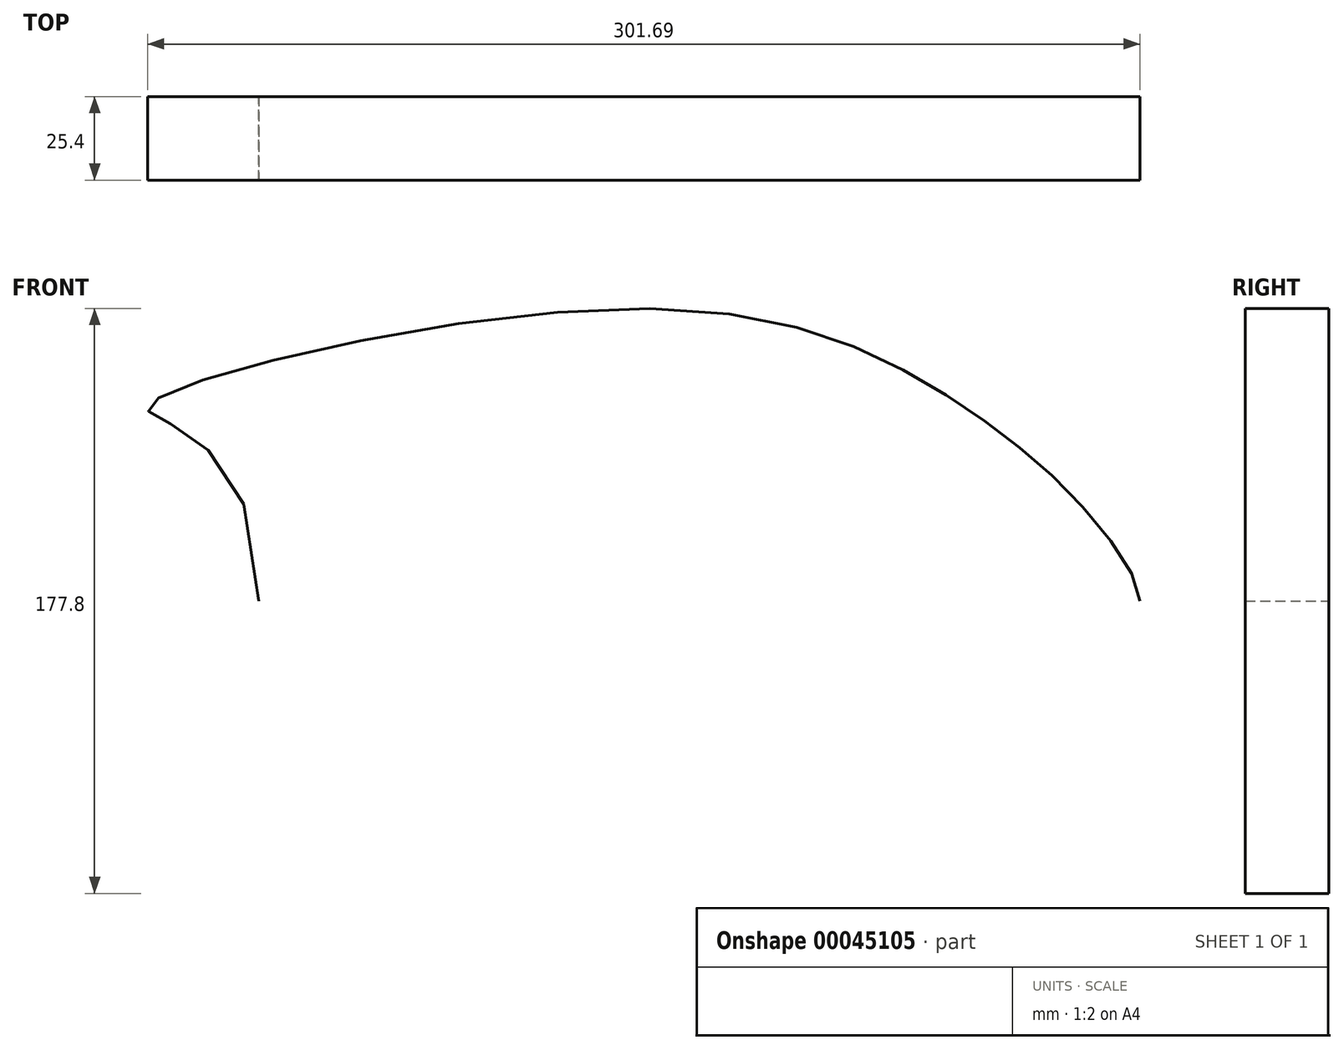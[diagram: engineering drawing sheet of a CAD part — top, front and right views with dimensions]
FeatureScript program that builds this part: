
annotation { "Feature Type Name" : "Feature", "Feature Type Description" : "" }
export const myFeature = defineFeature(function(context is Context, id is Id, definition is map)
    precondition{}
    {
        {
            var Q0;
            Q0=qCreatedBy(makeId("Front.planeOp"),FACE);
            var sketch = newSketch(context, id + "F0", { "sketchPlane" : qUnion([Q0])});
            skLineSegment(sketch, "E0.rect.bottom", {"start": v(152.4, -101.6) * mm, "end": v(-152.4, -101.6) * mm, "construction": true});
            skLineSegment(sketch, "E0.rect.top", {"start": v(152.4, 101.6) * mm, "end": v(-152.4, 101.6) * mm, "construction": true});
            skLineSegment(sketch, "E0.rect.left", {"start": v(152.4, -101.6) * mm, "end": v(152.4, 101.6) * mm, "construction": true});
            skLineSegment(sketch, "E0.rect.right", {"start": v(-152.4, -101.6) * mm, "end": v(-152.4, 101.6) * mm, "construction": true});
            skPoint(sketch, "E0.rect.middle", {"position": v(0, 0) * mm});
            skLineSegment(sketch, "E1", {"start": v(0, 101.6) * mm, "end": v(0, -101.6) * mm, "construction": true});
            skFitSpline(sketch, "E2", {"points": [v(-115.46, 0) * mm, v(-149.21, 58.9) * mm, v(0, 88.9) * mm, v(95, 61.54) * mm, v(133.76, 29.86) * mm, v(152.4, 0) * mm], "startDerivative": vector(6.18, 858.11) * mm, "endDerivative": vector(0, -164) * mm});
            skFitSpline(sketch, "E3.MirrorCS", {"points": [v(-115.46, 0) * mm, v(-149.21, -58.9) * mm, v(0, -88.9) * mm, v(95, -61.54) * mm, v(133.76, -29.86) * mm, v(152.4, 0) * mm], "startDerivative": vector(6.18, -858.11) * mm, "endDerivative": vector(0, 164) * mm});
            skLineSegment(sketch, "E4", {"start": v(51.7, 29.86) * mm, "end": v(51.7, -29.86) * mm});
            skLineSegment(sketch, "E5", {"start": v(35.48, 29.86) * mm, "end": v(35.48, -29.86) * mm});
            skLineSegment(sketch, "E6", {"start": v(19.88, 29.86) * mm, "end": v(19.88, -29.86) * mm});
            skLineSegment(sketch, "E7", {"start": v(66.68, 29.86) * mm, "end": v(66.68, -29.86) * mm});
            skLineSegment(sketch, "E8", {"start": v(80.75, 29.86) * mm, "end": v(80.75, -29.86) * mm});
            skLineSegment(sketch, "E9", {"start": v(95, 29.86) * mm, "end": v(95, -29.86) * mm});
            skLineSegment(sketch, "E10", {"start": v(109.8, 29.86) * mm, "end": v(109.8, -29.86) * mm});
            skLineSegment(sketch, "E11", {"start": v(123.27, 29.86) * mm, "end": v(123.27, -29.86) * mm});
            skLineSegment(sketch, "E12", {"start": v(6.75, 29.86) * mm, "end": v(6.75, -29.86) * mm});
            skLineSegment(sketch, "E13", {"start": v(-9.18, -29.86) * mm, "end": v(-9.18, 29.86) * mm});
            skLineSegment(sketch, "E14", {"start": v(-25.08, -29.86) * mm, "end": v(-25.08, 29.86) * mm});
            skLineSegment(sketch, "E15", {"start": v(-39.15, -29.86) * mm, "end": v(-39.15, 29.86) * mm});
            skLineSegment(sketch, "E16", {"start": v(-51.7, -29.86) * mm, "end": v(-51.7, 29.86) * mm});
            skLineSegment(sketch, "E17", {"start": v(-65.15, -29.86) * mm, "end": v(-65.15, 29.86) * mm});
            skLineSegment(sketch, "E18", {"start": v(-79.83, -29.86) * mm, "end": v(-79.83, 29.86) * mm});
            skLineSegment(sketch, "E19", {"start": v(-93.9, -29.86) * mm, "end": v(-93.9, 29.86) * mm});
            skLineSegment(sketch, "E20", {"start": v(-106.14, -29.86) * mm, "end": v(-106.14, 29.86) * mm});
            skLineSegment(sketch, "E21.right", {"start": v(-51.7, -32.42) * mm, "end": v(-51.7, 0) * mm});
            skSolve(sketch);
        }
        {
            var Q0;
            {var subQ0=sQuery(id+"F0.wireOp",EDGE,"3eca18d6-078a-4532-b09b-61f9cdbd6ef5");Q0=makeQuery(id+"F0.imprint","IMPRINT",FACE,{"disambiguationData":[TD([[makeQuery(id+"F0.imprint","IMPRINT",EDGE,{"derivedFrom":subQ0}),-1.0]])]});}
            var Q1;
            {var subQ1=sQuery(id+"F0.wireOp",EDGE,"E3.MirrorCS");Q1=makeQuery(id+"F0.imprint","IMPRINT",FACE,{"disambiguationData":[TD([[makeQuery(id+"F0.imprint","IMPRINT",EDGE,{"derivedFrom":subQ1}),1.0]])]});}
            extrude(context, id + "F1", {"entities" : qUnion([Q0, Q1]), "depth" : 25.4 * mm});
        }
    });
